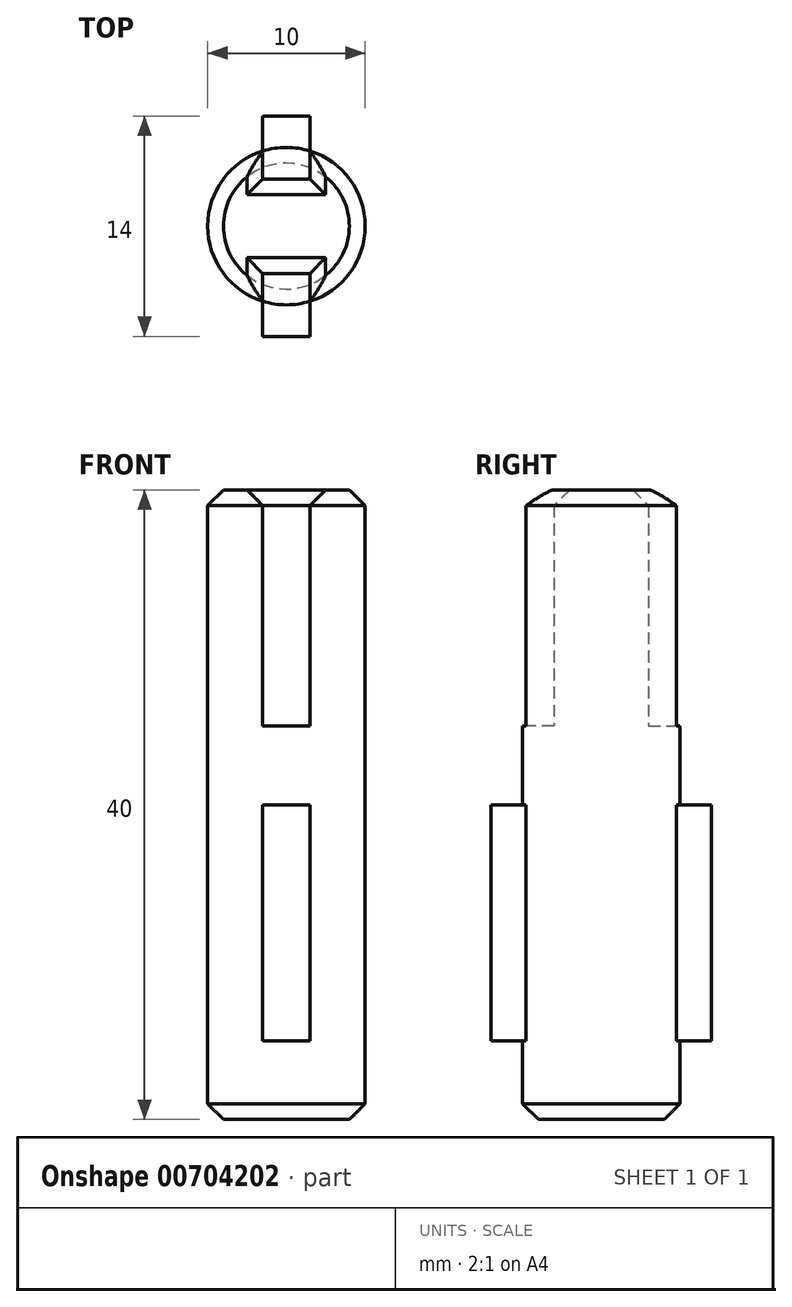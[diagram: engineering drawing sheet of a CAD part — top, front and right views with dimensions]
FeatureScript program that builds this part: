
annotation { "Feature Type Name" : "Feature", "Feature Type Description" : "" }
export const myFeature = defineFeature(function(context is Context, id is Id, definition is map)
    precondition{}
    {
        {
            var Q0;
            Q0=qCreatedBy(makeId("Top.planeOp"),FACE);
            var sketch = newSketch(context, id + "F0", { "sketchPlane" : qUnion([Q0])});
            skCircle(sketch, "E0", {"center": v(0, 0) * mm, "radius": 5 * mm});
            skSolve(sketch);
        }
        {
            var Q0;
            Q0=makeQuery(id+"F0.imprint","IMPRINT",FACE,{"disambiguationData":[TD([[makeQuery(id+"F0.imprint","IMPRINT",EDGE,{"derivedFrom":sQuery(id+"F0.wireOp",EDGE,"E0")}),1.0]])]});
            extrude(context, id + "F1", {"entities" : qUnion([Q0]), "depth" : 5 * mm, "offsetDistance" : 25 * mm});
        }
        {
            var Q0;
            Q0=makeQuery(id+"F1.opExtrude","CAP_FACE",FACE,{"disambiguationData":[OSD([sQuery(id+"F0.wireOp",EDGE,"E0")])],"isStart":false});
            var sketch = newSketch(context, id + "F2", { "sketchPlane" : qUnion([Q0])});
            skArc(sketch, "E1", {"start": v(-1.5, 4.77) * mm, "mid": v(-5, 0) * mm, "end": v(-1.5, -4.77) * mm});
            skLineSegment(sketch, "E2.bottom", {"start": v(1.5, 7) * mm, "end": v(-1.5, 7) * mm});
            skLineSegment(sketch, "E2.top", {"start": v(1.5, -7) * mm, "end": v(-1.5, -7) * mm});
            skLineSegment(sketch, "E2.left", {"start": v(1.5, 7) * mm, "end": v(1.5, 4.77) * mm});
            skLineSegment(sketch, "E2.right", {"start": v(-1.5, 7) * mm, "end": v(-1.5, 4.77) * mm});
            skLineSegment(sketch, "E3.trimOffspring", {"start": v(-1.5, -4.77) * mm, "end": v(-1.5, -7) * mm});
            skLineSegment(sketch, "E4.trimOffspring", {"start": v(1.5, -4.77) * mm, "end": v(1.5, -7) * mm});
            skArc(sketch, "E5.trimOffspring", {"start": v(1.5, -4.77) * mm, "mid": v(5, 0) * mm, "end": v(1.5, 4.77) * mm});
            skSolve(sketch);
        }
        {
            var Q0;
            Q0=qSketchRegion(id+"F2",true);
            extrude(context, id + "F3", {"entities" : qUnion([Q0]), "operationType" : NewBodyOperationType.ADD, "depth" : 15 * mm, "offsetDistance" : 25 * mm});
        }
        {
            var Q0;
            Q0=makeQuery(id+"F3.opExtrude","CAP_FACE",FACE,{"disambiguationData":[OSD([sQuery(id+"F2.wireOp",EDGE,"E1"),sQuery(id+"F2.wireOp",EDGE,"E2.bottom"),sQuery(id+"F2.wireOp",EDGE,"E2.top"),sQuery(id+"F2.wireOp",EDGE,"E2.left"),sQuery(id+"F2.wireOp",EDGE,"E2.right"),sQuery(id+"F2.wireOp",EDGE,"E3.trimOffspring"),sQuery(id+"F2.wireOp",EDGE,"E4.trimOffspring"),sQuery(id+"F2.wireOp",EDGE,"E5.trimOffspring")])],"isStart":false});
            var sketch = newSketch(context, id + "F4", { "sketchPlane" : qUnion([Q0])});
            skCircle(sketch, "E6", {"center": v(0, 0) * mm, "radius": 5 * mm});
            skSolve(sketch);
        }
        {
            var Q0;
            {var subQ0=sQuery(id+"F4.wireOp",EDGE,"E6");var subQ1=makeQuery(id+"F4.imprint","INTERSECT",VERTEX,{"derivedFrom":[makeQuery(id+"F3.opExtrude","CAP_EDGE",EDGE,{"disambiguationData":[OSD([sQuery(id+"F2.wireOp",EDGE,"E2.right")])],"isStart":false}),subQ0]});Q0=makeQuery(id+"F4.imprint","IMPRINT",FACE,{"disambiguationData":[TD([[makeQuery(id+"F4.imprint","IMPRINT",EDGE,{"disambiguationData":[TD([[subQ1,1.0]])],"derivedFrom":subQ0}),1.0]])]});}
            extrude(context, id + "F5", {"entities" : qUnion([Q0]), "operationType" : NewBodyOperationType.ADD, "depth" : 5 * mm, "offsetDistance" : 25 * mm});
        }
        {
            var Q0;
            Q0=makeQuery(id+"F5.opExtrude","CAP_FACE",FACE,{"disambiguationData":[OSD([sQuery(id+"F4.wireOp",EDGE,"E6")])],"isStart":false});
            var sketch = newSketch(context, id + "F6", { "sketchPlane" : qUnion([Q0])});
            skArc(sketch, "E7", {"start": v(1.5, -4.77) * mm, "mid": v(5, 0) * mm, "end": v(1.5, 4.77) * mm});
            skLineSegment(sketch, "E8", {"start": v(0, 5) * mm, "end": v(0, -5) * mm, "construction": true});
            skLineSegment(sketch, "E9", {"start": v(-1.5, 3) * mm, "end": v(1.5, 3) * mm});
            skPoint(sketch, "E10", {"position": v(0, 3) * mm});
            skLineSegment(sketch, "E11", {"start": v(-1.5, 3) * mm, "end": v(-1.5, 4.77) * mm});
            skLineSegment(sketch, "E12", {"start": v(1.5, 3) * mm, "end": v(1.5, 4.77) * mm});
            skLineSegment(sketch, "E13", {"start": v(5, 0) * mm, "end": v(-5, 0) * mm, "construction": true});
            skLineSegment(sketch, "E14.MirrorCS", {"start": v(-1.5, -3) * mm, "end": v(1.5, -3) * mm});
            skLineSegment(sketch, "E15.MirrorCS", {"start": v(1.5, -3) * mm, "end": v(1.5, -4.77) * mm});
            skLineSegment(sketch, "E16.MirrorCS", {"start": v(-1.5, -3) * mm, "end": v(-1.5, -4.77) * mm});
            skArc(sketch, "E17.trimOffspring", {"start": v(-1.5, 4.77) * mm, "mid": v(-5, 0) * mm, "end": v(-1.5, -4.77) * mm});
            skSolve(sketch);
        }
        {
            var Q0;
            Q0=qSketchRegion(id+"F6",true);
            extrude(context, id + "F7", {"entities" : qUnion([Q0]), "operationType" : NewBodyOperationType.ADD, "depth" : 15 * mm, "offsetDistance" : 25 * mm});
        }
        {
            var Q0;
            Q0=makeQuery(id+"F1.opExtrude","CAP_FACE",FACE,{"disambiguationData":[OSD([sQuery(id+"F0.wireOp",EDGE,"E0")])],"isStart":true});
            var Q1;
            Q1=makeQuery(id+"F7.opExtrude","CAP_FACE",FACE,{"disambiguationData":[OSD([sQuery(id+"F6.wireOp",EDGE,"E7"),sQuery(id+"F6.wireOp",EDGE,"E9"),sQuery(id+"F6.wireOp",EDGE,"E11"),sQuery(id+"F6.wireOp",EDGE,"E12"),sQuery(id+"F6.wireOp",EDGE,"E14.MirrorCS"),sQuery(id+"F6.wireOp",EDGE,"E15.MirrorCS"),sQuery(id+"F6.wireOp",EDGE,"E16.MirrorCS"),sQuery(id+"F6.wireOp",EDGE,"E17.trimOffspring")])],"isStart":false});
            chamfer(context, id + "F8", {"entities" : qUnion([Q0, Q1]), "width" : 1 * mm, "tangentPropagation" : true});
        }
    });
